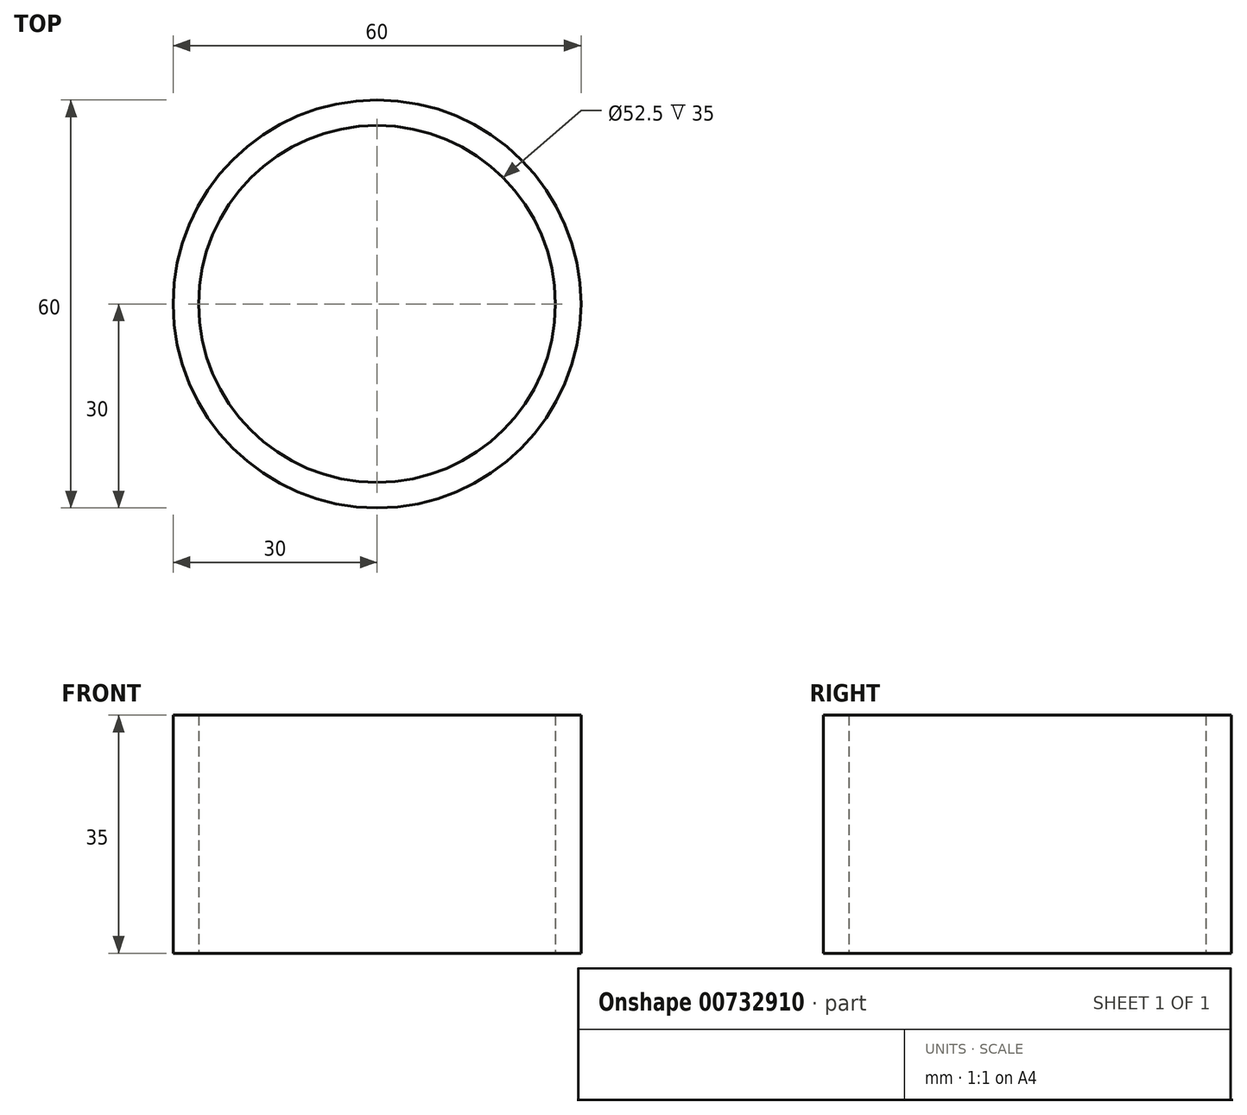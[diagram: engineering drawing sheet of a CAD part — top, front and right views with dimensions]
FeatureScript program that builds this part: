
annotation { "Feature Type Name" : "Feature", "Feature Type Description" : "" }
export const myFeature = defineFeature(function(context is Context, id is Id, definition is map)
    precondition{}
    {
        {
            var Q0;
            Q0=qCreatedBy(makeId("Top.planeOp"),FACE);
            var sketch = newSketch(context, id + "F0", { "sketchPlane" : qUnion([Q0])});
            skCircle(sketch, "E0", {"center": v(0, 0) * mm, "radius": 30 * mm});
            skCircle(sketch, "E1", {"center": v(0, 0) * mm, "radius": 26.25 * mm});
            skSolve(sketch);
        }
        {
            var Q0;
            Q0=makeQuery(id+"F0.imprint","IMPRINT",FACE,{"disambiguationData":[TD([[makeQuery(id+"F0.imprint","IMPRINT",EDGE,{"derivedFrom":sQuery(id+"F0.wireOp",EDGE,"E0")}),1.0]])]});
            extrude(context, id + "F1", {"entities" : qUnion([Q0]), "depth" : 35 * mm, "offsetDistance" : 25 * mm});
        }
    });
